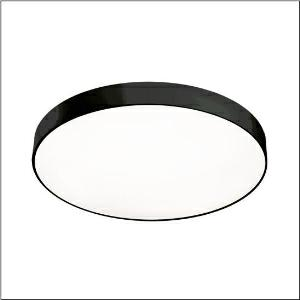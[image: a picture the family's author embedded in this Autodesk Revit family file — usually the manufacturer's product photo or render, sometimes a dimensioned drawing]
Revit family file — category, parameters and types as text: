
# Revit family: round_21_l_51mr38fd0321b
name_source: partatom
category: Lighting Fixtures
units: mm (PartAtom-declared; Revit-internal decimal feet)

## family parameters
Cut with Voids When Loaded = No
Host = Face
Light Source = No
Part Type = Normal
Room Calculation Point = No
Round Connector Dimension = Use Diameter
Shared = No

## types (1)
- Round 21 L (1 x LED, 13590 lm, 97 W, 3000K)
    Apparent Load = 97 VA
    CIE Flux Codes = 49 80 96 100 100
    Color Rendering = 80
    Color Temperature = 3000K
    Default Elevation = 1800 mm
    Description = Round 21 L, wall and ceiling luminaire, primary optical cover: cover, of PMMA, opal, light emission: direct distribution, primary light characteristic: symmetric, installation type: suspended mounting, surface-mounted, LED, rated luminous flux: 13.590lm, luminous efficacy: 140lm/W, light colour: 830, colour temperature: 3000K, control gear: DALI 2, with terminal, 5-pole, mains connection: 230V, AC, 50/60Hz, rated input power: 97W, housing, of aluminium, coated, black, diameter: 850mm, height: 62mm, protection rating (complete): IP40, insulation class (complete): insulation class I (protective earthing), certification: CE, impact resistance: IK04, permissible operating ambient temperature: -10..+35°C, packaging unit: 1 piece
    Height = 87 mm
    Lamp = 1 x LED
    Lamp Light Flux = 13590 lm
    Lamp Power = 97 W
    Lamp count = 1
    Length = 850 mm
    Luminous efficacy = 140 lm/W
    Manufacturer = Siteco
    ModVariant = No
    Model = 51MR38FD0321B
    Mounting Place = Ceiling
    Mounting Type = Surface mounted
    Number of Poles = 1
    OnlyDefault = Yes
    Power Factor = 1
    Product Name = Round 21 L
    Product group = wall and ceiling luminaire | ceiling mounted
    ProductGroupID = 304
    Protection Class = Protection class I
    Protection Degree = IP 40
    RLX_Detail_Level = 1
    RLX_Emergency_Light_Flux = 0 lm
    RLX_Emergency_Type = 0
    RLX_Emergency_Type_DB = No
    RlxData = <blob elided: 23933 chars, md5=ce702479>
    Socket = socket
    Standby Power = 0 W
    System Light Flux = 13590 lm
    System Power = 97 W
    Type Comments = Product without accessories
    Type Image = l_1258328.jpg
    URL = http://relux.com
    VarID = ---
    Voltage = 0 V
    Weight = 0.00 kg
    Width = 0 mm  [stored 0 ft]

note: [stored X ft] marks values corroborated as IEEE doubles in the binary element streams (Revit-internal decimal feet)

## geometry (parser evidence)
native form markers: Blend x4, Sweep x9
no freeform markers — native parametric forms only
